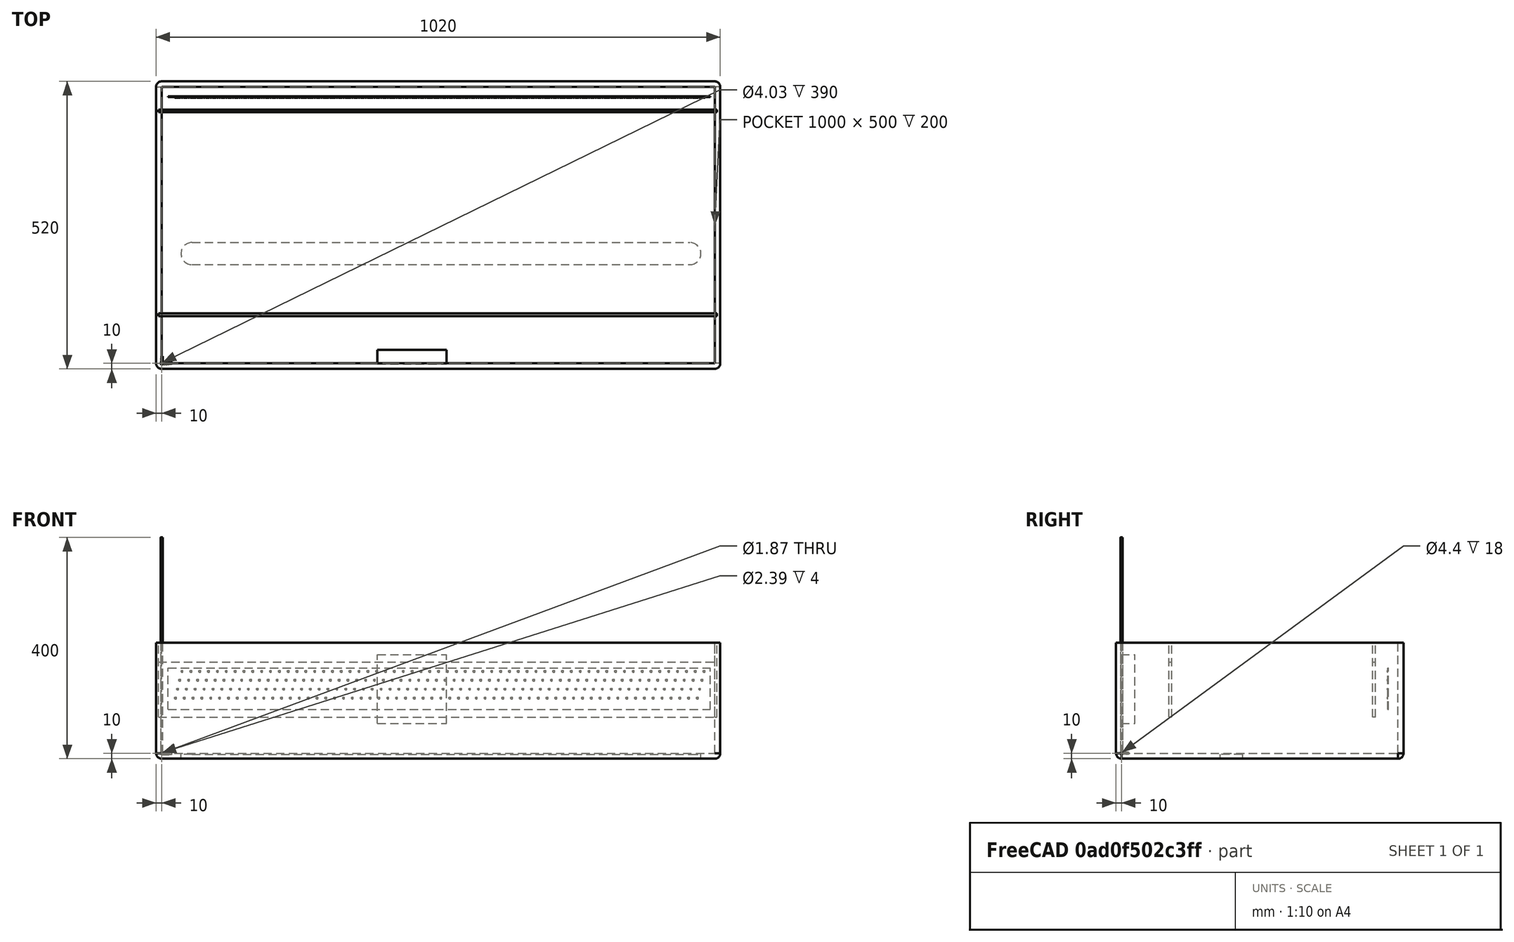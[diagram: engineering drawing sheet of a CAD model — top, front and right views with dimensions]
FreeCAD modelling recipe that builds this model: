
FCSTD DOCUMENT  (FreeCAD 0.19R23074 (Git))
Label: Box
License: All rights reserved
LicenseURL: http://en.wikipedia.org/wiki/All_rights_reserved
objects: Part::Box×9, Part::Part2DObjectPython×8, Part::Compound×5, Part::Sweep×4, App::Part×4, Part::Cut×3, Part::Feature×3, Part::FeaturePython×2, Part::Cylinder×2, Part::Thickness×1, Part::MultiFuse×1
note: 36 computed .brp shape members not serialized (recipe doc carries the construction recipe); baked Part::Feature solids carry a one-line shape summary decoded from their .brp

FEATURE [Part::Box] Box  label="Cube"
  AttacherType = Attacher::AttachEngine3D
  Height = 200
  Length = 1000
  Width = 500
FEATURE [Part::Thickness] Thickness  label="Box"
  Faces = -> Box [Face6]
  Intersection = false
  Join = 0
  Mode = 0
  SelfIntersection = false
  Value = 10
FEATURE [Part::Box] Box001  label="Support001"
  AttacherType = Attacher::AttachEngine3D
  Height = 100
  Length = 1010
  Placement = pos=(-5.7935,85.5,65) rot=(0,0,1;0rad)
  Width = 5
FEATURE [Part::Box] Box002  label="Support002"
  AttacherType = Attacher::AttachEngine3D
  Height = 100
  Length = 1010
  Placement = pos=(-5.7935,454,65) rot=(0,0,1;0rad)
  Width = 5
FEATURE [Part::Box] Box007  label="CalibLEDBox"
  AttacherType = Attacher::AttachEngine3D
  Height = 25
  Length = 125
  Placement = pos=(390.26,-0.9,53.5) rot=(0.57735,0.57735,0.57735;4.18879rad)
  Width = 125
FEATURE [Part::Part2DObjectPython] BezCurve  # Draft 2D object (typed FeaturePython)
  Area = 0
  Closed = false
  Degree = 3
  Length = 133.246
  MakeFace = true
  Points = (4) [(37.73,178.199,85.1424),(15,143.338,83.3527),(-3.29845,149.367,143.96),(39.5292,81.953,149.244)]
FEATURE [Part::Part2DObjectPython] Circle001  # Draft 2D object (typed FeaturePython)
  Area = 0.785398
  FirstAngle = 0
  LastAngle = 0
  MakeFace = true
  Placement = pos=(39.5292,81.953,149.244) rot=(-0.540873,0.659298,0.522286;3.71755rad)
  Radius = 0.5
FEATURE [Part::Sweep] Sweep  label="OpticFiber"
  Frenet = false
  Placement = pos=(-83.0642,-149.15,32.7197) rot=(-0.889126,-0.323616,-0.323616;1.68804rad)
  Sections = -> [Circle001]
  Solid = false
  Spine = -> BezCurve [Edge1]
  Transition = 1
FEATURE [Part::Compound] Compound001  label="Fiber001"
  Links = -> [Sweep]
  Placement = pos=(538,81,98.5) rot=(0.57735,0.57735,0.57735;4.18879rad)
FEATURE [Part::Part2DObjectPython] Circle002  # Draft 2D object (typed FeaturePython)
  Area = 0.785398
  FirstAngle = 0
  LastAngle = 0
  MakeFace = true
  Placement = pos=(39.5292,81.953,149.244) rot=(-0.540873,0.659298,0.522286;3.71755rad)
  Radius = 0.5
FEATURE [Part::Part2DObjectPython] BezCurve001  # Draft 2D object (typed FeaturePython)
  Area = 0
  Closed = false
  Degree = 3
  Length = 133.246
  MakeFace = true
  Points = (4) [(37.73,178.199,85.1424),(15,143.338,83.3527),(-3.29845,149.367,143.96),(39.5292,81.953,149.244)]
FEATURE [Part::Sweep] Sweep001  label="OpticFiber002"
  Frenet = false
  Placement = pos=(-83.0642,-149.15,32.7197) rot=(-0.889126,-0.323616,-0.323616;1.68804rad)
  Sections = -> [Circle002]
  Solid = false
  Spine = -> BezCurve001 [Edge1]
  Transition = 1
FEATURE [Part::Compound] Compound002  label="Fiber002"
  Links = -> [Sweep001]
  Placement = pos=(553.7,81,98.2) rot=(0.57735,0.57735,0.57735;4.18879rad)
FEATURE [Part::Part2DObjectPython] Circle003  # Draft 2D object (typed FeaturePython)
  Area = 0.785398
  FirstAngle = 0
  LastAngle = 0
  MakeFace = true
  Placement = pos=(39.5292,81.953,149.244) rot=(-0.540873,0.659298,0.522286;3.71755rad)
  Radius = 0.5
FEATURE [Part::Part2DObjectPython] BezCurve002  # Draft 2D object (typed FeaturePython)
  Area = 0
  Closed = false
  Degree = 3
  Length = 133.246
  MakeFace = true
  Points = (4) [(37.73,178.199,85.1424),(15,143.338,83.3527),(-3.29845,149.367,143.96),(39.5292,81.953,149.244)]
FEATURE [Part::Sweep] Sweep002  label="OpticFiber003"
  Frenet = false
  Placement = pos=(-83.0642,-149.15,32.7197) rot=(-0.889126,-0.323616,-0.323616;1.68804rad)
  Sections = -> [Circle003]
  Solid = false
  Spine = -> BezCurve002 [Edge1]
  Transition = 1
FEATURE [Part::Compound] Compound003  label="Fiber003"
  Links = -> [Sweep002]
  Placement = pos=(558,81,115) rot=(0.57735,0.57735,0.57735;4.18879rad)
FEATURE [Part::Part2DObjectPython] Circle004  # Draft 2D object (typed FeaturePython)
  Area = 0.785398
  FirstAngle = 0
  LastAngle = 0
  MakeFace = true
  Placement = pos=(39.5292,81.953,149.244) rot=(-0.540873,0.659298,0.522286;3.71755rad)
  Radius = 0.5
FEATURE [Part::Part2DObjectPython] BezCurve003  # Draft 2D object (typed FeaturePython)
  Area = 0
  Closed = false
  Degree = 3
  Length = 133.246
  MakeFace = true
  Points = (4) [(37.73,178.199,85.1424),(15,143.338,83.3527),(-3.29845,149.367,143.96),(39.5292,81.953,149.244)]
FEATURE [Part::Sweep] Sweep003  label="OpticFiber004"
  Frenet = false
  Placement = pos=(-83.0642,-149.15,32.7197) rot=(-0.889126,-0.323616,-0.323616;1.68804rad)
  Sections = -> [Circle004]
  Solid = false
  Spine = -> BezCurve003 [Edge1]
  Transition = 1
FEATURE [Part::Compound] Compound004  label="Fiber004"
  Links = -> [Sweep003]
  Placement = pos=(542,81,115) rot=(0.57735,0.57735,0.57735;4.18879rad)
FEATURE [Part::Box] Box008  label="SiPM"
  AttacherType = Attacher::AttachEngine3D
  Height = 3
  Length = 3
  Width = 1
FEATURE [Part::FeaturePython] Array001  label="SiPM001"  # Draft array (typed FeaturePython)
  Angle = 360
  ArrayType = 0
  Axis = (0,0,1)
  Base = -> Box008
  Center = (0,0,0)
  Count = 240
  ExpandArray = false
  Fuse = false
  IntervalAxis = (0,0,0)
  IntervalX = (16,0,0)
  IntervalY = (4,0,16)
  IntervalZ = (0,0,100)
  NumberCircles = 3
  NumberPolar = 5
  NumberX = 60
  NumberY = 4
  NumberZ = 1
  Placement = pos=(23.5,479,98.5) rot=(0,0,1;0rad)
  PlacementList = 240 placements: [(0,0,0),(4,0,16),(8,0,32),(12,0,48),(16,0,0),(20,0,16),(24,0,32),(28,0,48),(32,0,0),(36,0,16),(40,0,32),(44,0,48),(48,0,0),(52,0,16),(56,0,32),(60,0,48),(64,0,0),(68,0,16),(72,0,32),(76,0,48),(80,0,0),(84,0,16),(88,0,32),(92,0,48),(96,0,0),(100,0,16),(104,0,32),(108,0,48),(112,0,0),(116,0,16),(120,0,32),(124,0,48),(128,0,0),(132,0,16),(136,0,32),(140,0,48),(144,0,0),(148,0,16),(152,0,32),+201 more]
  RadialDistance = 50
  ScaleList = (240) [(1,1,1),(1,1,1),(1,1,1),(1,1,1),(1,1,1),(1,1,1),(1,1,1),(1,1,1),(1,1,1),(1,1,1),(1,1,1),(1,1,1),(1,1,1),(1,1,1),(1,1,1),(1,1,1),(1,1,1),(1,1,1),+222 more]
  Symmetry = 1
  TangentialDistance = 25
FEATURE [Part::Box] Box009  label="PCB"
  AttacherType = Attacher::AttachEngine3D
  Height = 75
  Length = 980
  Placement = pos=(11.7065,480,79) rot=(0,0,1;0rad)
  Width = 1
FEATURE [Part::Compound] Compound  label="PCBSiPM"
  Links = -> [Box009,Array001]
  Placement = pos=(0,1.6,0) rot=(0,0,1;0rad)
FEATURE [Part::Box] Box010  label="SupportRail001"
  AttacherType = Attacher::AttachEngine3D
  Height = 200
  Length = 1010
  Placement = pos=(-5.7935,454,65) rot=(0,0,1;0rad)
  Width = 5
FEATURE [Part::Box] Box011  label="SupportRail002"
  AttacherType = Attacher::AttachEngine3D
  Height = 200
  Length = 1010
  Placement = pos=(-5.7935,85.5,65) rot=(0,0,1;0rad)
  Width = 5
FEATURE [Part::Cut] Cut
  Base = -> Thickness
  Tool = -> Box010
FEATURE [Part::Cut] Cut001  label="BoxAll"
  Base = -> Cut
  Tool = -> Box011
FEATURE [Part::Cylinder] Cylinder004
  Angle = 360
  AttacherType = Attacher::AttachEngine3D
  Height = 9.5
  Placement = pos=(1.5,955,139) rot=(0,-1,0;1.5708rad)
  Radius = 20
FEATURE [Part::Cylinder] Cylinder003
  Angle = 360
  AttacherType = Attacher::AttachEngine3D
  Height = 9.5
  Placement = pos=(1.5,55,139) rot=(0,-1,0;1.5708rad)
  Radius = 20
FEATURE [Part::Box] Box012  label="Cube002"
  AttacherType = Attacher::AttachEngine3D
  Height = 40
  Length = 9.5
  Placement = pos=(-8,55,119) rot=(0,0,1;0rad)
  Width = 900
FEATURE [Part::MultiFuse] Fusion  label="Windows"
  Placement = pos=(7.5e-14,337.5,-10) rot=(0.57735,0.57735,-0.57735;2.0944rad)
  Refine = true
  Shapes = -> [Cylinder003,Box012,Cylinder004]
FEATURE [Part::Cut] Cut002  label="CherenkovBox"
  Base = -> Cut001
  Tool = -> Fusion
FEATURE [Part::Feature] Part__Feature003  label="SmallEndCapModel"
  shape: bbox 4.6 x 13 x 4.6 mm, 17 faces (baked)
FEATURE [Part::Feature] Part__Feature004  label="BigEndcapModel"
  shape: bbox 18 x 5.9 x 5.9 mm, 16 faces (baked)
FEATURE [App::Part] SmallEndCap001
  Group = -> [Part__Feature003]
  Origin = -> Origin005
  Placement = pos=(0,0,-8.5) rot=(1,0,0;1.5708rad)
FEATURE [Part::Feature] Part__Feature005  label="StrawTubeModel001"
  shape: bbox 4.15 x 4.15 x 390 mm, 4 faces (baked)
FEATURE [App::Part] StrawTube001
  Group = -> [Part__Feature005]
  Origin = -> Origin
FEATURE [App::Part] BigEndCap001
  Group = -> [Part__Feature004]
  Origin = -> Origin006
  Placement = pos=(0,0,405.5) rot=(0,1,0;1.5708rad)
FEATURE [App::Part] Straw
  Group = -> [StrawTube001,SmallEndCap001,BigEndCap001]
  Origin = -> Origin007
  Placement = pos=(0,0,0) rot=(1,0,0;4.71239rad)
FEATURE [Part::FeaturePython] Array002  label="ArrayStraws"  # Draft array (typed FeaturePython)
  Angle = 360
  ArrayType = 0
  Axis = (0,0,1)
  Base = -> Straw
  Center = (0,0,0)
  Count = 240
  ExpandArray = false
  Fuse = false
  IntervalAxis = (0,0,0)
  IntervalX = (16,0,0)
  IntervalY = (4,0,16)
  IntervalZ = (0,0,100)
  NumberCircles = 3
  NumberPolar = 5
  NumberX = 60
  NumberY = 4
  NumberZ = 1
  Placement = pos=(25,75,100) rot=(0,0,1;0rad)
  PlacementList = 240 placements: [(0,0,0),(4,0,16),(8,0,32),(12,0,48),(16,0,0),(20,0,16),(24,0,32),(28,0,48),(32,0,0),(36,0,16),(40,0,32),(44,0,48),(48,0,0),(52,0,16),(56,0,32),(60,0,48),(64,0,0),(68,0,16),(72,0,32),(76,0,48),(80,0,0),(84,0,16),(88,0,32),(92,0,48),(96,0,0),(100,0,16),(104,0,32),(108,0,48),(112,0,0),(116,0,16),(120,0,32),(124,0,48),(128,0,0),(132,0,16),(136,0,32),(140,0,48),(144,0,0),(148,0,16),(152,0,32),+201 more]
  RadialDistance = 50
  ScaleList = (240) [(1,1,1),(1,1,1),(1,1,1),(1,1,1),(1,1,1),(1,1,1),(1,1,1),(1,1,1),(1,1,1),(1,1,1),(1,1,1),(1,1,1),(1,1,1),(1,1,1),(1,1,1),(1,1,1),(1,1,1),(1,1,1),+222 more]
  Symmetry = 1
  TangentialDistance = 25
